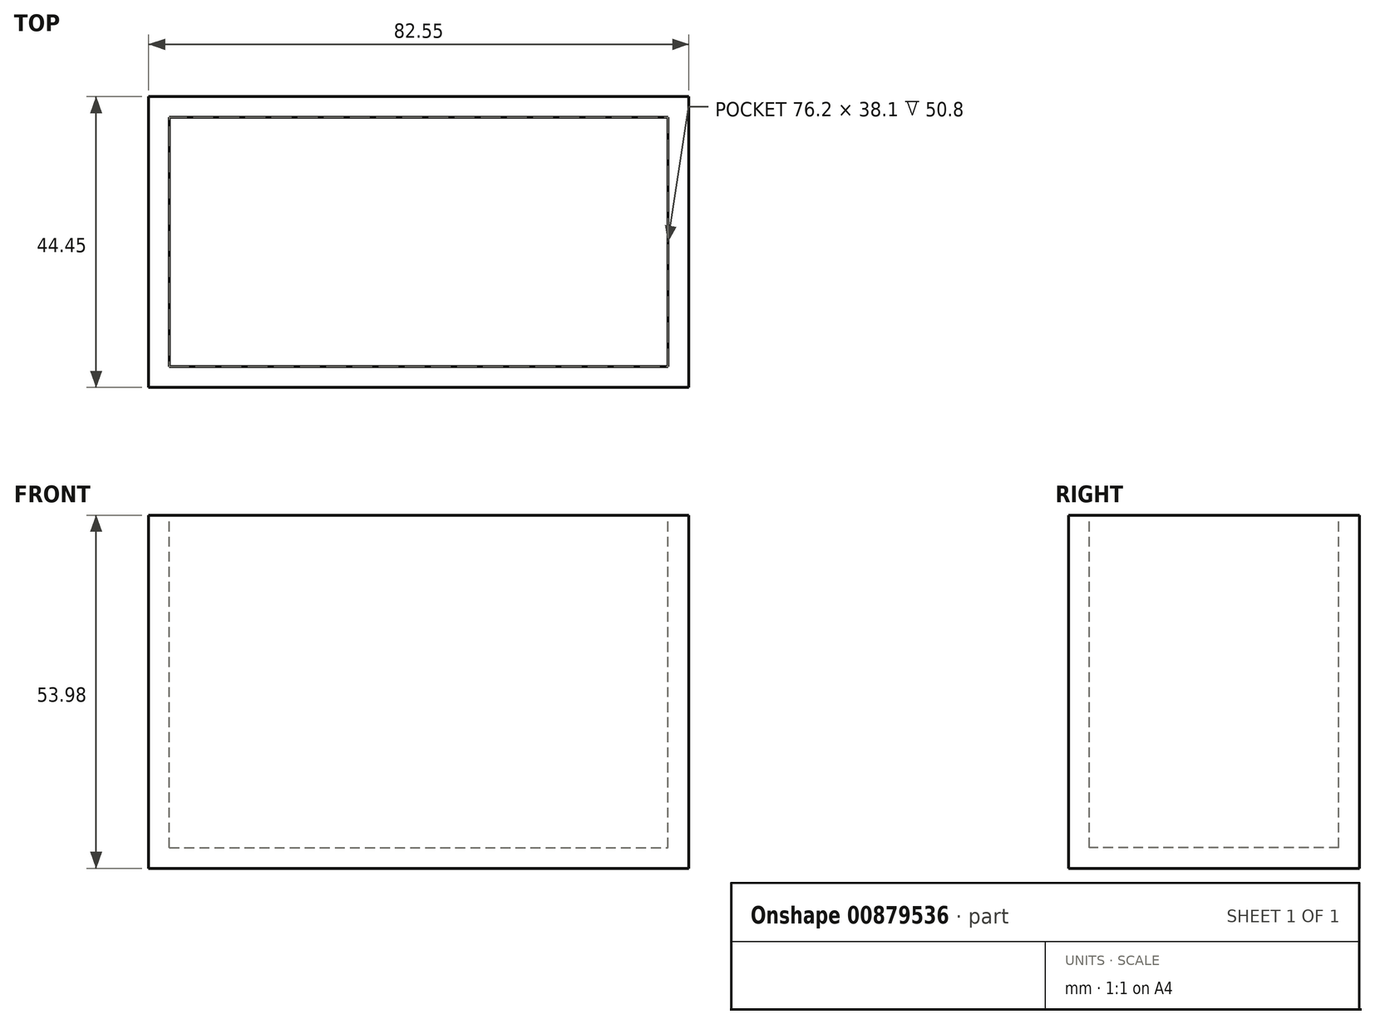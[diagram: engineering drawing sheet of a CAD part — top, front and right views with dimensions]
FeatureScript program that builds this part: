
annotation { "Feature Type Name" : "Feature", "Feature Type Description" : "" }
export const myFeature = defineFeature(function(context is Context, id is Id, definition is map)
    precondition{}
    {
        {
            var Q0;
            Q0=qCreatedBy(makeId("Top.planeOp"),FACE);
            var sketch = newSketch(context, id + "F0", { "sketchPlane" : qUnion([Q0])});
            skLineSegment(sketch, "E0.bottom", {"start": v(-36.26, 28.22) * mm, "end": v(39.94, 28.22) * mm});
            skLineSegment(sketch, "E0.top", {"start": v(-36.26, -9.88) * mm, "end": v(39.94, -9.88) * mm});
            skLineSegment(sketch, "E0.left", {"start": v(-36.26, 28.22) * mm, "end": v(-36.26, -9.88) * mm});
            skLineSegment(sketch, "E0.right", {"start": v(39.94, 28.22) * mm, "end": v(39.94, -9.88) * mm});
            skSolve(sketch);
        }
        {
            var Q0;
            Q0=qCreatedBy(makeId("Top.planeOp"),FACE);
            var sketch = newSketch(context, id + "F1", { "sketchPlane" : qUnion([Q0])});
            skLineSegment(sketch, "E1.bottom", {"start": v(-39.43, 31.4) * mm, "end": v(43.12, 31.4) * mm});
            skLineSegment(sketch, "E1.top", {"start": v(-39.43, -13.05) * mm, "end": v(43.12, -13.05) * mm});
            skLineSegment(sketch, "E1.left", {"start": v(-39.43, 31.4) * mm, "end": v(-39.43, -13.05) * mm});
            skLineSegment(sketch, "E1.right", {"start": v(43.12, 31.4) * mm, "end": v(43.12, -13.05) * mm});
            skSolve(sketch);
        }
        {
            var Q0;
            Q0 = qSketchRegion(id + "F1", true);
            extrude(context, id + "F2", {"entities" : qUnion([Q0]), "depth" : 53.97 * mm, "offsetDistance" : 25.4 * mm});
        }
        {
            var Q0;
            Q0=makeQuery(id+"F2.opExtrude","CAP_FACE",FACE,{"disambiguationData":[OSD([sQuery(id+"F1.wireOp",EDGE,"E1.bottom"),sQuery(id+"F1.wireOp",EDGE,"E1.top"),sQuery(id+"F1.wireOp",EDGE,"E1.left"),sQuery(id+"F1.wireOp",EDGE,"E1.right")])],"isStart":false});
            var sketch = newSketch(context, id + "F3", { "sketchPlane" : qUnion([Q0])});
            skLineSegment(sketch, "E2.bottom", {"start": v(-36.26, 28.22) * mm, "end": v(39.94, 28.22) * mm});
            skLineSegment(sketch, "E2.top", {"start": v(-36.26, -9.88) * mm, "end": v(39.94, -9.88) * mm});
            skLineSegment(sketch, "E2.left", {"start": v(-36.26, 28.22) * mm, "end": v(-36.26, -9.88) * mm});
            skLineSegment(sketch, "E2.right", {"start": v(39.94, 28.22) * mm, "end": v(39.94, -9.88) * mm});
            skSolve(sketch);
        }
        {
            var Q0;
            Q0=makeQuery(id+"F3.imprint","IMPRINT",FACE,{"disambiguationData":[TD([[makeQuery(id+"F3.imprint","IMPRINT",EDGE,{"derivedFrom":sQuery(id+"F3.wireOp",EDGE,"E2.bottom")}),-1.0]])]});
            extrude(context, id + "F4", {"entities" : qUnion([Q0]), "operationType" : NewBodyOperationType.REMOVE, "oppositeDirection" : true, "depth" : 50.8 * mm, "offsetDistance" : 25.4 * mm});
        }
    });
